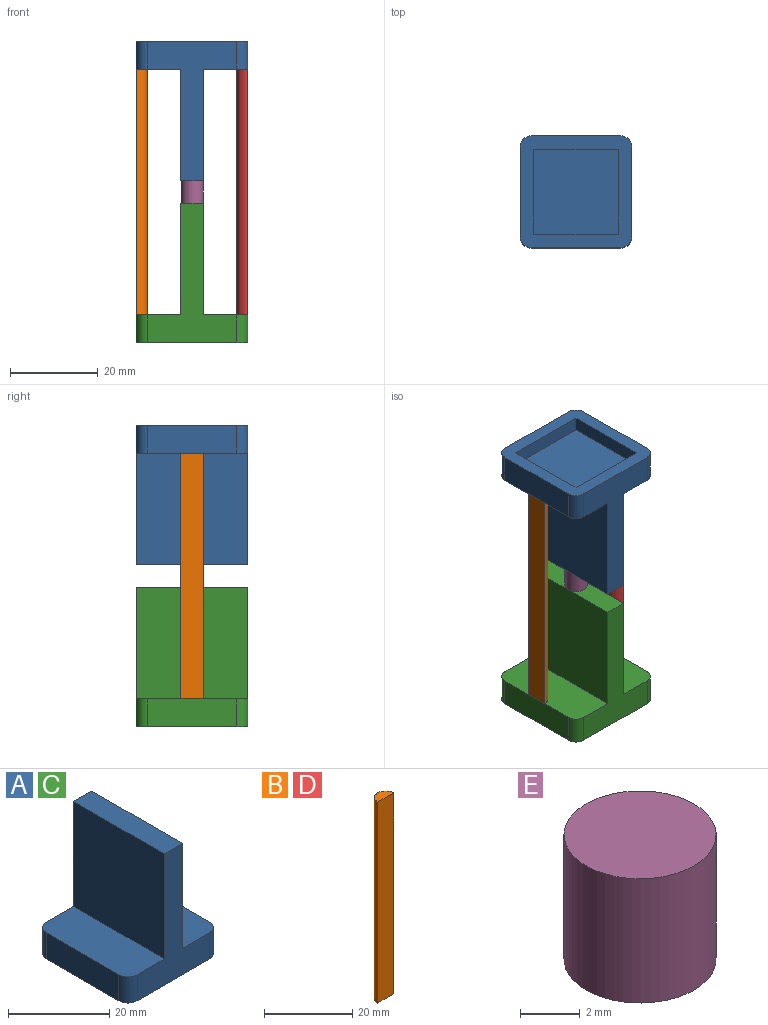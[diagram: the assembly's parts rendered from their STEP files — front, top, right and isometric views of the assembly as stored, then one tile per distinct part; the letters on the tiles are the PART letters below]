
ASSEMBLY  parts=5 mates=6
PART A: 19 faces, bbox 25.4x25.4x31.8 mm
  f0: plane 25.4x10.16mm, normal (0,0,1), area 255.3mm2, adj f1,f2,f4,f7,f10,f17
  f1: plane 20.32x6.35mm, normal (1,0,0), area 129mm2, adj f0,f6,f7,f10
  f2: plane 31.75x20.32mm, normal (0,1,0), area 258.1mm2, adj f0,f5,f6,f7,f8,f16,f17,f18
  f3: plane 20.32x6.35mm, normal (-1,0,0), area 129mm2, adj f5,f6,f8,f9
  f4: plane 31.75x20.32mm, normal (0,-1,0), area 258.1mm2, adj f0,f5,f6,f9,f10,f16,f17,f18
  f5: plane 25.4x10.16mm, normal (0,0,1), area 255.3mm2, adj f2,f3,f4,f8,f9,f16
  f6: plane 25.4x25.4mm, normal (0,0,-1), area 267mm2, adj f1,f2,f3,f4,f7,f8,f9,f10
  f7: cylinder r=2.54mm len=6.35mm, axis (0,0,1), area 25.3mm2, adj f0,f1,f2,f6
  f8: cylinder r=2.54mm len=6.35mm, axis (0,0,-1), area 25.3mm2, adj f2,f3,f5,f6
  f9: cylinder r=2.54mm len=6.35mm, axis (0,0,1), area 25.3mm2, adj f3,f4,f5,f6
  f10: cylinder r=2.54mm len=6.35mm, axis (0,0,-1), area 25.3mm2, adj f0,f1,f4,f6
  f11: plane 19.3x3.3mm, normal (-1,0,0), area 63.7mm2, adj f6,f12,f14,f15
  f12: plane 19.3x3.3mm, normal (0,-1,0), area 63.7mm2, adj f6,f11,f13,f15
  f13: plane 19.3x3.3mm, normal (1,0,0), area 63.7mm2, adj f6,f12,f14,f15
  f14: plane 19.3x3.3mm, normal (0,1,0), area 63.7mm2, adj f6,f11,f13,f15
  f15: plane 19.3x19.3mm, normal (0,0,-1), area 372.6mm2, adj f11,f12,f13,f14
  f16: plane 25.4x25.4mm, normal (-1,0,0), area 645.2mm2, adj f2,f4,f5,f18
  f17: plane 25.4x25.4mm, normal (1,0,0), area 645.2mm2, adj f0,f2,f4,f18
  f18: plane 25.4x5.08mm, normal (0,0,1), area 129mm2, adj f2,f4,f16,f17
PART B: 4 faces, bbox 5.1x2.5x55.9 mm
  f0: plane 55.88x5.08mm, normal (0,-1,0), area 283.9mm2, adj f1,f2,f3
  f1: cylinder r=2.54mm len=55.88mm, axis (0,0,-1), area 445.9mm2, adj f0,f2,f3
  f2: plane 5.08x2.54mm, normal (0,0,1), area 10.1mm2, adj f0,f1
  f3: plane 5.08x2.54mm, normal (0,0,-1), area 10.1mm2, adj f0,f1
PART C: same geometry as A
PART D: same geometry as B
PART E: 3 faces, bbox 5.1x5.1x5.1 mm
  f0: cylinder r=2.54mm len=5.08mm, axis (0,0,-1), area 81.1mm2, adj f1,f2
  f1: plane 5.08x5.08mm, normal (0,0,1), area 20.3mm2, adj f0
  f2: plane 5.08x5.08mm, normal (0,0,-1), area 20.3mm2, adj f0
PLACE A rot(axis=(1,0,0),180deg) t=(-160.72,25.48,-16.12)mm
PLACE B rot(axis=(0,0,-1),90deg) t=(32.89,-23,-78.35)mm
PLACE C t=(-160.72,25.48,-84.7)mm
PLACE D rot(axis=(0,0,1),90deg) t=(26.67,73.95,-78.35)mm
PLACE E rot(axis=(1,0,0),180deg) t=(59.84,31.37,-47.87)mm
MATE fastened E.f0 <-> C.f18  axis (0,0,-1) through (29.78,25.48,-52.95)mm
MATE fastened D.f1 <-> A.f0  axis (0,0,1) through (42.48,25.48,-22.47)mm
MATE fastened A.f5 <-> B.f1  axis (0,0,-1) through (17.08,25.48,-22.47)mm
MATE fastened A.f18 <-> E.f0  axis (0,0,-1) through (29.78,25.48,-47.87)mm
MATE planar D.f0 <-> A.f1  axis (1,0,0) through (42.48,25.48,-50.41)mm
MATE planar B.f0 <-> A.f3  axis (-1,0,0) through (17.08,25.48,-50.41)mm
